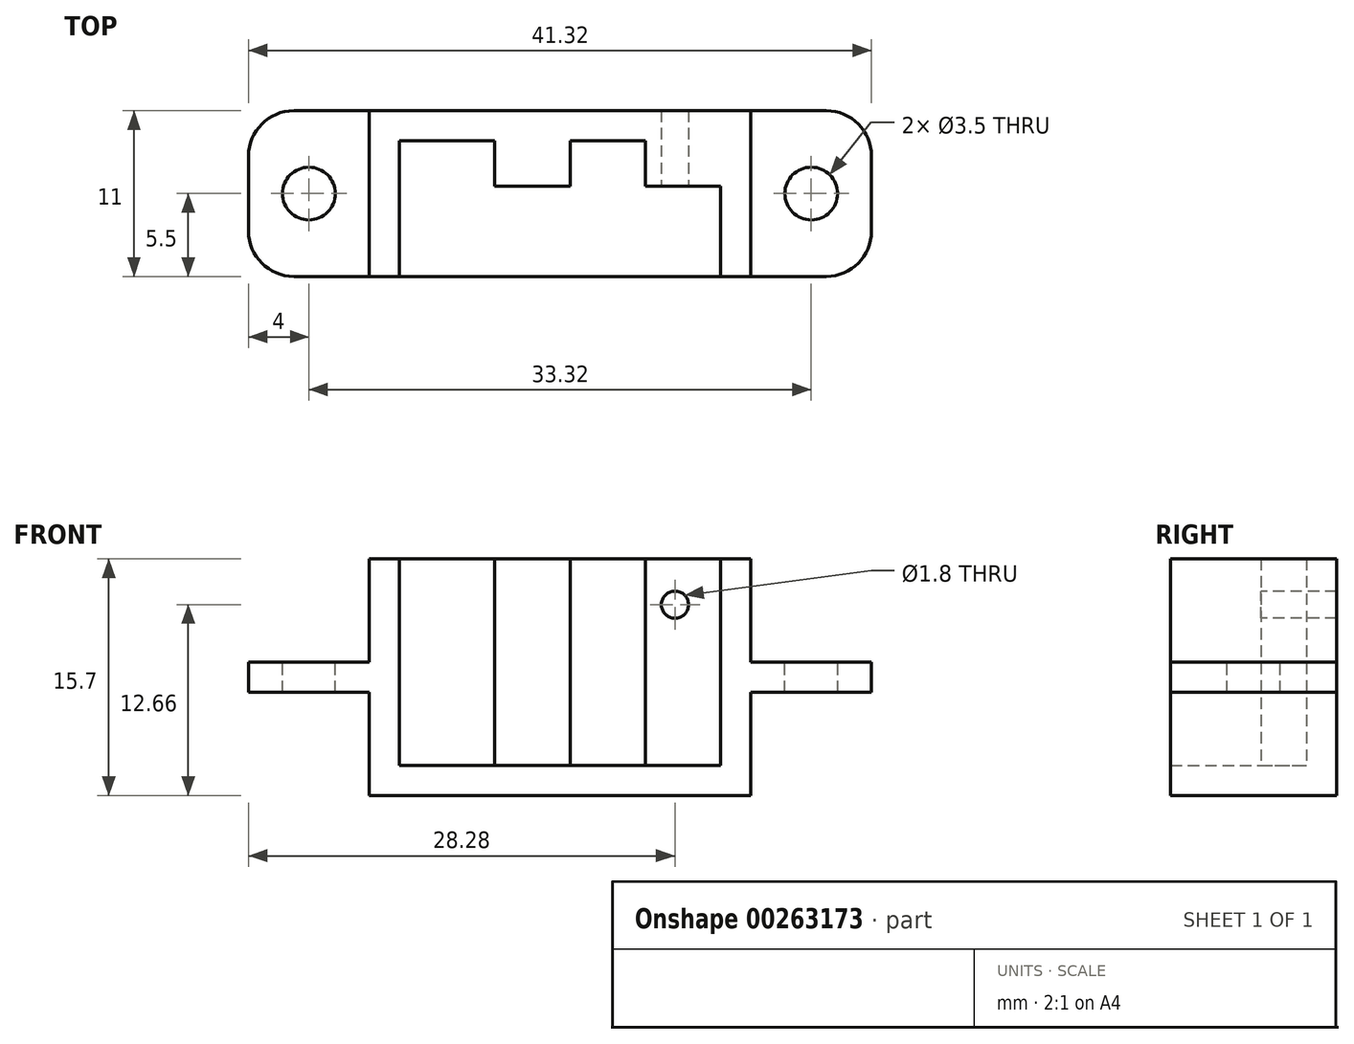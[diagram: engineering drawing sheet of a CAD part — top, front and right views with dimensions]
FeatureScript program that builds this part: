
annotation { "Feature Type Name" : "Feature", "Feature Type Description" : "" }
export const myFeature = defineFeature(function(context is Context, id is Id, definition is map)
    precondition{}
    {
        {
            var Q0;
            Q0=qCreatedBy(makeId("Front.planeOp"),FACE);
            var sketch = newSketch(context, id + "F0", { "sketchPlane" : qUnion([Q0])});
            skLineSegment(sketch, "E0.bottom", {"start": v(0, 0) * mm, "end": v(20.32, 0) * mm, "construction": true});
            skLineSegment(sketch, "E0.top", {"start": v(0, 12.7) * mm, "end": v(20.32, 12.7) * mm, "construction": true});
            skLineSegment(sketch, "E0.left", {"start": v(0, 0) * mm, "end": v(0, 12.7) * mm, "construction": true});
            skLineSegment(sketch, "E0.right", {"start": v(20.32, 0) * mm, "end": v(20.32, 12.7) * mm, "construction": true});
            skCircle(sketch, "E1", {"center": v(17.78, 10.16) * mm, "radius": 1.1 * mm, "construction": true});
            skLineSegment(sketch, "E2.bottom", {"start": v(-2.5, 13.2) * mm, "end": v(22.82, 13.2) * mm});
            skLineSegment(sketch, "E2.top", {"start": v(-2.5, -2.5) * mm, "end": v(22.82, -2.5) * mm});
            skLineSegment(sketch, "E2.left", {"start": v(-2.5, 13.2) * mm, "end": v(-2.5, -2.5) * mm});
            skLineSegment(sketch, "E2.right", {"start": v(22.82, 13.2) * mm, "end": v(22.82, -2.5) * mm});
            skSolve(sketch);
        }
        {
            var Q0;
            Q0 = qSketchRegion(id + "F0", true);
            extrude(context, id + "F1", {"entities" : qUnion([Q0]), "depth" : 2 * mm});
        }
        {
            var Q0;
            Q0=makeQuery(id+"F1.opExtrude","CAP_FACE",FACE,{"disambiguationData":[OSD([sQuery(id+"F0.wireOp",EDGE,"E2.bottom"),sQuery(id+"F0.wireOp",EDGE,"E2.top"),sQuery(id+"F0.wireOp",EDGE,"E2.left"),sQuery(id+"F0.wireOp",EDGE,"E2.right")])],"isStart":false});
            var sketch = newSketch(context, id + "F2", { "sketchPlane" : qUnion([Q0])});
            skLineSegment(sketch, "E3.top", {"start": v(-2.5, -2.5) * mm, "end": v(22.82, -2.5) * mm});
            skLineSegment(sketch, "E3.left", {"start": v(-2.5, 13.2) * mm, "end": v(-2.5, -2.5) * mm});
            skLineSegment(sketch, "E3.right", {"start": v(22.82, 13.2) * mm, "end": v(22.82, -2.5) * mm});
            skLineSegment(sketch, "E4.top", {"start": v(-0.5, -0.5) * mm, "end": v(20.82, -0.5) * mm});
            skLineSegment(sketch, "E4.left", {"start": v(-0.5, 13.2) * mm, "end": v(-0.5, -0.5) * mm});
            skLineSegment(sketch, "E4.right", {"start": v(20.82, 13.2) * mm, "end": v(20.82, -0.5) * mm});
            skLineSegment(sketch, "E5", {"start": v(-2.5, 13.2) * mm, "end": v(-0.5, 13.2) * mm});
            skLineSegment(sketch, "E6", {"start": v(22.82, 13.2) * mm, "end": v(20.82, 13.2) * mm});
            skSolve(sketch);
        }
        {
            var Q0;
            Q0 = qSketchRegion(id + "F2", true);
            extrude(context, id + "F3", {"entities" : qUnion([Q0]), "operationType" : NewBodyOperationType.ADD, "depth" : 9 * mm});
        }
        {
            var Q0;
            Q0=makeQuery(id+"F1.opExtrude","CAP_FACE",FACE,{"disambiguationData":[OSD([sQuery(id+"F0.wireOp",EDGE,"E2.bottom"),sQuery(id+"F0.wireOp",EDGE,"E2.top"),sQuery(id+"F0.wireOp",EDGE,"E2.left"),sQuery(id+"F0.wireOp",EDGE,"E2.right")])],"isStart":false});
            var sketch = newSketch(context, id + "F4", { "sketchPlane" : qUnion([Q0])});
            skLineSegment(sketch, "E7.top", {"start": v(5.82, -0.5) * mm, "end": v(10.82, -0.5) * mm});
            skLineSegment(sketch, "E7.left", {"start": v(5.82, 13.2) * mm, "end": v(5.82, -0.5) * mm});
            skLineSegment(sketch, "E7.right", {"start": v(10.82, 13.2) * mm, "end": v(10.82, -0.5) * mm});
            skLineSegment(sketch, "E8", {"start": v(5.82, 13.2) * mm, "end": v(10.82, 13.2) * mm});
            skLineSegment(sketch, "E9.bottom", {"start": v(15.82, 13.2) * mm, "end": v(20.82, 13.2) * mm});
            skLineSegment(sketch, "E9.top", {"start": v(15.82, -0.5) * mm, "end": v(20.82, -0.5) * mm});
            skLineSegment(sketch, "E9.left", {"start": v(15.82, 13.2) * mm, "end": v(15.82, -0.5) * mm});
            skLineSegment(sketch, "E9.right", {"start": v(20.82, 13.2) * mm, "end": v(20.82, -0.5) * mm});
            skSolve(sketch);
        }
        {
            var Q0;
            Q0 = qSketchRegion(id + "F4", true);
            extrude(context, id + "F5", {"entities" : qUnion([Q0]), "operationType" : NewBodyOperationType.ADD, "depth" : 3 * mm});
        }
        {
            var Q0;
            Q0=makeQuery(id+"F5.opExtrude","CAP_FACE",FACE,{"disambiguationData":[OSD([sQuery(id+"F4.wireOp",EDGE,"E9.bottom"),sQuery(id+"F4.wireOp",EDGE,"E9.top"),sQuery(id+"F4.wireOp",EDGE,"E9.left"),sQuery(id+"F4.wireOp",EDGE,"E9.right")])],"isStart":false});
            var sketch = newSketch(context, id + "F6", { "sketchPlane" : qUnion([Q0])});
            skCircle(sketch, "E10", {"center": v(17.78, 10.16) * mm, "radius": 0.9 * mm});
            skSolve(sketch);
        }
        {
            var Q0;
            Q0 = qSketchRegion(id + "F6", true);
            extrude(context, id + "F7", {"entities" : qUnion([Q0]), "operationType" : NewBodyOperationType.REMOVE, "endBound" : BoundingType.THROUGH_ALL, "oppositeDirection" : true, "depth" : 25 * mm});
        }
        {
            var Q0;
            Q0=makeQuery(id+"F3.boolean.opBoolean","MERGE",FACE,{"derivedFrom":[makeQuery(id+"F1.opExtrude","SWEPT_FACE",FACE,{"disambiguationData":[OSD([sQuery(id+"F0.wireOp",EDGE,"E2.left")])]}),makeQuery(id+"F3.opExtrude","SWEPT_FACE",FACE,{"disambiguationData":[OSD([sQuery(id+"F2.wireOp",EDGE,"E3.left")])]})]});
            var sketch = newSketch(context, id + "F8", { "sketchPlane" : qUnion([Q0])});
            skLineSegment(sketch, "E11", {"start": v(0, 5.35) * mm, "end": v(11, 5.35) * mm, "construction": true});
            skLineSegment(sketch, "E12.bottom", {"start": v(0, 6.35) * mm, "end": v(11, 6.35) * mm});
            skLineSegment(sketch, "E12.top", {"start": v(0, 4.35) * mm, "end": v(11, 4.35) * mm});
            skLineSegment(sketch, "E12.left", {"start": v(0, 6.35) * mm, "end": v(0, 4.35) * mm});
            skLineSegment(sketch, "E12.right", {"start": v(11, 6.35) * mm, "end": v(11, 4.35) * mm});
            skSolve(sketch);
        }
        {
            var Q0;
            Q0 = qSketchRegion(id + "F8", true);
            extrude(context, id + "F9", {"entities" : qUnion([Q0]), "operationType" : NewBodyOperationType.ADD, "depth" : 8 * mm});
        }
        {
            var Q0;
            Q0=makeQuery(id+"F9.opExtrude","CAP_EDGE",EDGE,{"disambiguationData":[OSD([sQuery(id+"F8.wireOp",EDGE,"E12.right")])],"isStart":false});
            var Q1;
            Q1=makeQuery(id+"F9.opExtrude","CAP_EDGE",EDGE,{"disambiguationData":[OSD([sQuery(id+"F8.wireOp",EDGE,"E12.left")])],"isStart":false});
            fillet(context, id + "F10", {"entities" : qUnion([Q0, Q1]), "radius" : 3 * mm, "tangentPropagation" : true, "allowEdgeOverflow" : false});
        }
        {
            var Q0;
            Q0=makeQuery(id+"F3.boolean.opBoolean","MERGE",FACE,{"derivedFrom":[makeQuery(id+"F1.opExtrude","SWEPT_FACE",FACE,{"disambiguationData":[OSD([sQuery(id+"F0.wireOp",EDGE,"E2.right")])]}),makeQuery(id+"F3.opExtrude","SWEPT_FACE",FACE,{"disambiguationData":[OSD([sQuery(id+"F2.wireOp",EDGE,"E3.right")])]})]});
            var sketch = newSketch(context, id + "F11", { "sketchPlane" : qUnion([Q0])});
            skLineSegment(sketch, "E13", {"start": v(-11, 5.35) * mm, "end": v(0, 5.35) * mm, "construction": true});
            skLineSegment(sketch, "E14.bottom", {"start": v(-11, 6.35) * mm, "end": v(0, 6.35) * mm});
            skLineSegment(sketch, "E14.top", {"start": v(-11, 4.35) * mm, "end": v(0, 4.35) * mm});
            skLineSegment(sketch, "E14.left", {"start": v(-11, 6.35) * mm, "end": v(-11, 4.35) * mm});
            skLineSegment(sketch, "E14.right", {"start": v(0, 6.35) * mm, "end": v(0, 4.35) * mm});
            skSolve(sketch);
        }
        {
            var Q0;
            Q0 = qSketchRegion(id + "F11", true);
            extrude(context, id + "F12", {"entities" : qUnion([Q0]), "operationType" : NewBodyOperationType.ADD, "depth" : 8 * mm});
        }
        {
            var Q0;
            Q0=makeQuery(id+"F12.opExtrude","CAP_EDGE",EDGE,{"disambiguationData":[OSD([sQuery(id+"F11.wireOp",EDGE,"E14.left")])],"isStart":false});
            var Q1;
            Q1=makeQuery(id+"F12.opExtrude","CAP_EDGE",EDGE,{"disambiguationData":[OSD([sQuery(id+"F11.wireOp",EDGE,"E14.right")])],"isStart":false});
            fillet(context, id + "F13", {"entities" : qUnion([Q0, Q1]), "radius" : 3 * mm, "tangentPropagation" : true, "allowEdgeOverflow" : false});
        }
        {
            var Q0;
            Q0=makeQuery(id+"F9.opExtrude","SWEPT_FACE",FACE,{"disambiguationData":[OSD([sQuery(id+"F8.wireOp",EDGE,"E12.bottom")])]});
            var sketch = newSketch(context, id + "F14", { "sketchPlane" : qUnion([Q0])});
            skLineSegment(sketch, "E15", {"start": v(-10.5, -5.5) * mm, "end": v(-2.5, -5.5) * mm, "construction": true});
            skCircle(sketch, "E16", {"center": v(-6.5, -5.5) * mm, "radius": 1.75 * mm});
            skSolve(sketch);
        }
        {
            var Q0;
            Q0 = qSketchRegion(id + "F14", true);
            extrude(context, id + "F15", {"entities" : qUnion([Q0]), "operationType" : NewBodyOperationType.REMOVE, "endBound" : BoundingType.THROUGH_ALL, "oppositeDirection" : true, "depth" : 25 * mm});
        }
        {
            var Q0;
            Q0=makeQuery(id+"F12.opExtrude","SWEPT_FACE",FACE,{"disambiguationData":[OSD([sQuery(id+"F11.wireOp",EDGE,"E14.bottom")])]});
            var sketch = newSketch(context, id + "F16", { "sketchPlane" : qUnion([Q0])});
            skLineSegment(sketch, "E17", {"start": v(22.82, -5.5) * mm, "end": v(30.82, -5.5) * mm, "construction": true});
            skCircle(sketch, "E18", {"center": v(26.82, -5.5) * mm, "radius": 1.75 * mm});
            skSolve(sketch);
        }
        {
            var Q0;
            Q0 = qSketchRegion(id + "F16", true);
            extrude(context, id + "F17", {"entities" : qUnion([Q0]), "operationType" : NewBodyOperationType.REMOVE, "endBound" : BoundingType.THROUGH_ALL, "oppositeDirection" : true, "depth" : 25 * mm});
        }
    });
